# Revit family: PRD_AR_SftyShwrs_EmergencyCombinedBodyShower_FAID0011
name_source: partatom
category: Plumbing Fixtures
revit_build: Autodesk Revit 2018 (Build: 20190510_1515(x64)
units: mm (PartAtom-declared; Revit-internal decimal feet)

## family parameters
Cut with Voids When Loaded = Yes
Host = Face
OmniClass Number = 23.45.05.14.99
OmniClass Title = Other Sanitary Washing Plumbing Fixtures
Part Type = Normal
Room Calculation Point = No
Round Connector Dimension = Use Diameter
Shared = Yes

## types (1)
- FAID0011
    AssetType = Fixed
    BIMObjectName = PRD_AR_SafetyShowers_EmergencyCombinedBodyShower_FAID0011
    Category = Pr_40_20_27_75, Safety showers
    Color = green
    Default Elevation = 2300 mm
    Description = Combined emergency body shower and eye-wash fountain, for surface mounting, for water supply from the wall. Can be used independently of each other. Valve operation of showerhead by triangular handle, hand shower operated by pressing the white trigger button. Neither function self-closing. Water flow stopped by pushing the pull rod up or, with the eye-wash fountain, by pressing the red water stop button. Wall bracket and emergency shower head. Eye-wash fountain with device for precise positioning, inclined 20° forward, with spiral hose for flexible or stationary use. With an integrated flow regulator for a constant water spray height, non-return valve, grit filter and dust cap with user instructions. Surface body shower, green EPS coated (RAL 6032), eye-wash fountain, plastic, green with white trigger button. Complies with EN 15154, Part 1 and 2, includes the emergency shower and eye washing facility safety symbol on an adhesive label in compliance with ISO 3864, Part 1. Volumetric flow rate body shower: approx. 65 l/min at 1 bar pressure, approx. 110 l/min at 3 bar pressure, Volume flow rate eye-wash fountain: 9 l/min from 1 bar pressure upwards, Water connection: G 3/4 B
    DiameterNominal = 20  [stored 0.0656168 ft]
    DrainSize = 20 mm  [stored 0.0656168 ft]
    DripPan = No
    DurationUnit = year
    Features = Combined emergency body shower and eye-wash fountain
    Finish = EPS coated
    GrossWeight = 15.00 kg
    HasTray = FALSE
    IfcExportAs = IfcSanitaryTerminalType
    IfcExportType = SHOWER
    Manufacturer = KWC Group AG
    ManufacturerName = KWC Group AG
    ManufacturerURL = www.kwc.com
    Material = brass
    Model = FAID0011
    ModelNumber = 2030019221
    ModelReference = FAID0011
    Name = Emergency combined body shower FAID0011
    NetWeight = 14.00 kg
    NominalDepth = 0 mm  [stored 0 ft]
    NominalHeight = 0 mm  [stored 0 ft]
    NominalWidth = 0 mm  [stored 0 ft]
    ProductCode = 216.0540.432
    ProductInformation = https://pim.kwc.com
    ShowerHeadDescription = Emergency shower head
    ShowerMaterial = PRD_AR_Brass_EPSCoated_Green
    ShowerType = Individual
    SpoutProjection = 588.00 mm
    TypeOfConnection = Wall connection
    URL = www.kwc.com
    Uniclass2015Code = Pr_40_20_27_75
    Uniclass2015Title = Safety showers
    Uniclass2015Version = Products v1.17
    Version = 1
    VolumeFlowRate = 1.83 l/s at 3 bar
    WarrantyDurationUnit = year

note: [stored X ft] marks values corroborated as IEEE doubles in the binary element streams (Revit-internal decimal feet)

## geometry (parser evidence)
native form markers: Sweep x11
no freeform markers — native parametric forms only
